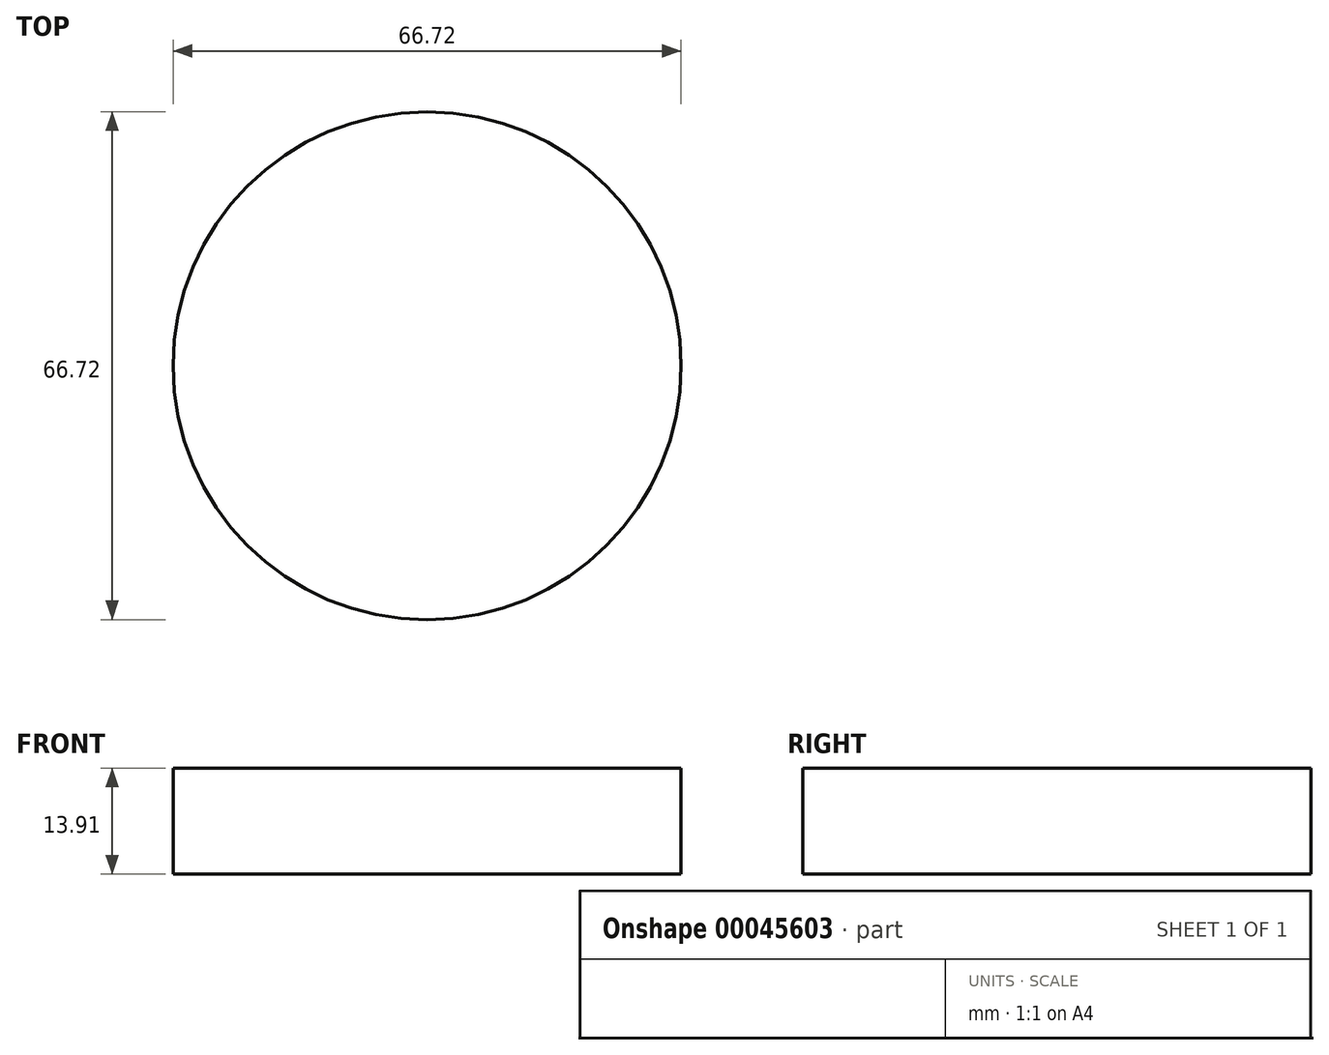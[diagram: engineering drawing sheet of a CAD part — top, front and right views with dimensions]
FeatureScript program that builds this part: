
annotation { "Feature Type Name" : "Feature", "Feature Type Description" : "" }
export const myFeature = defineFeature(function(context is Context, id is Id, definition is map)
    precondition{}
    {
        {
            var Q0;
            Q0=qCreatedBy(makeId("Top.planeOp"),FACE);
            var sketch = newSketch(context, id + "F0", { "sketchPlane" : qUnion([Q0])});
            skCircle(sketch, "E0", {"center": v(0, 0) * mm, "radius": 33.36 * mm});
            skSolve(sketch);
        }
        {
            var Q0;
            Q0=qSketchRegion(id+"F0",true);
            extrude(context, id + "F1", {"entities" : qUnion([Q0]), "depth" : 13.9 * mm});
        }
    });
